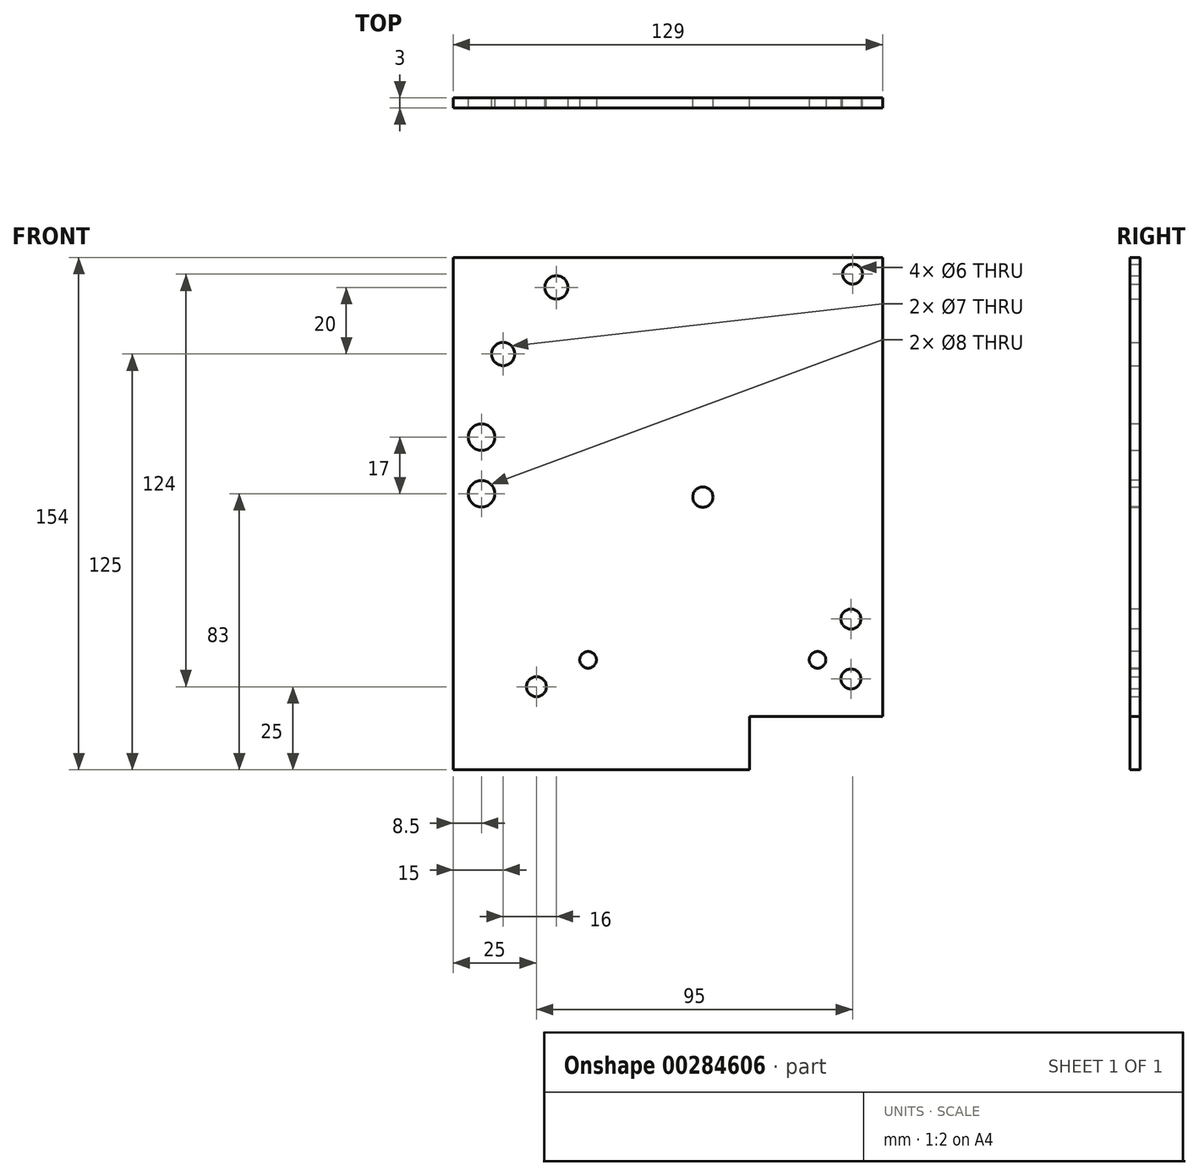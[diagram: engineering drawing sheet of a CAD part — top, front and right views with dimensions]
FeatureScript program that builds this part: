
annotation { "Feature Type Name" : "Feature", "Feature Type Description" : "" }
export const myFeature = defineFeature(function(context is Context, id is Id, definition is map)
    precondition{}
    {
        {
            var Q0;
            Q0=qCreatedBy(makeId("Front.planeOp"),FACE);
            var sketch = newSketch(context, id + "F0", { "sketchPlane" : qUnion([Q0])});
            skLineSegment(sketch, "E0", {"start": v(0, 0) * mm, "end": v(129, 0) * mm});
            skLineSegment(sketch, "E1", {"start": v(129, 0) * mm, "end": v(129, -138) * mm});
            skLineSegment(sketch, "E2", {"start": v(129, -138) * mm, "end": v(89, -138) * mm});
            skLineSegment(sketch, "E3", {"start": v(89, -138) * mm, "end": v(89, -154) * mm});
            skLineSegment(sketch, "E4", {"start": v(89, -154) * mm, "end": v(0, -154) * mm});
            skLineSegment(sketch, "E5", {"start": v(0, -154) * mm, "end": v(0, 0) * mm});
            skLineSegment(sketch, "E6", {"start": v(75, -154) * mm, "end": v(75, -127) * mm, "construction": true});
            skLineSegment(sketch, "E7", {"start": v(75, -127) * mm, "end": v(129, -127) * mm, "construction": true});
            skLineSegment(sketch, "E8", {"start": v(75, -127) * mm, "end": v(75, -72) * mm, "construction": true});
            skLineSegment(sketch, "E9", {"start": v(120, -138) * mm, "end": v(120, -99) * mm, "construction": true});
            skLineSegment(sketch, "E10", {"start": v(120, -99) * mm, "end": v(129, -99) * mm, "construction": true});
            skLineSegment(sketch, "E11", {"start": v(120, -99) * mm, "end": v(120, -5) * mm, "construction": true});
            skLineSegment(sketch, "E12", {"start": v(0, -9) * mm, "end": v(31, -9) * mm, "construction": true});
            skLineSegment(sketch, "E13", {"start": v(31, -9) * mm, "end": v(31, 0) * mm, "construction": true});
            skLineSegment(sketch, "E14", {"start": v(0, -29) * mm, "end": v(15, -29) * mm, "construction": true});
            skLineSegment(sketch, "E15", {"start": v(15, -29) * mm, "end": v(15, 0) * mm, "construction": true});
            skLineSegment(sketch, "E16", {"start": v(75, -129) * mm, "end": v(25, -129) * mm, "construction": true});
            skSolve(sketch);
        }
        {
            var Q0;
            Q0=makeQuery(id+"F0.imprint","IMPRINT",FACE,{"disambiguationData":[TD([[makeQuery(id+"F0.imprint","IMPRINT",EDGE,{"derivedFrom":sQuery(id+"F0.wireOp",EDGE,"E0")}),-1.0]])]});
            extrude(context, id + "F1", {"entities" : qUnion([Q0]), "depth" : 3 * mm});
        }
        {
            var Q0;
            Q0=sQuery(id+"F0.wireOp",VERTEX,"E14.end");
            var Q1;
            Q1=sQuery(id+"F0.wireOp",VERTEX,"E12.end");
            var Q2;
            Q2=makeQuery(id+"F1.opExtrude","SWEPT_BODY",BODY,{"disambiguationData":[OSD([sQuery(id+"F0.wireOp",EDGE,"E0"),sQuery(id+"F0.wireOp",EDGE,"E1"),sQuery(id+"F0.wireOp",EDGE,"E2"),sQuery(id+"F0.wireOp",EDGE,"E3"),sQuery(id+"F0.wireOp",EDGE,"E4"),sQuery(id+"F0.wireOp",EDGE,"E5")])]});
            hole(context, id + "F2", {"style" : HoleStyle.SIMPLE, "endStyle" : HoleEndStyle.THROUGH, "oppositeDirection" : true, "holeDiameter" : 7 * mm, "locations" : qUnion([Q0, Q1]), "scope" : qUnion([Q2]), "isTappedThrough" : true});
        }
        {
            var Q0;
            Q0=sQuery(id+"F0.wireOp",VERTEX,"E8.end");
            var Q1;
            Q1=makeQuery(id+"F1.opExtrude","SWEPT_BODY",BODY,{"disambiguationData":[OSD([sQuery(id+"F0.wireOp",EDGE,"E0"),sQuery(id+"F0.wireOp",EDGE,"E1"),sQuery(id+"F0.wireOp",EDGE,"E2"),sQuery(id+"F0.wireOp",EDGE,"E3"),sQuery(id+"F0.wireOp",EDGE,"E4"),sQuery(id+"F0.wireOp",EDGE,"E5")])]});
            hole(context, id + "F3", {"style" : HoleStyle.SIMPLE, "endStyle" : HoleEndStyle.THROUGH, "oppositeDirection" : true, "holeDiameter" : 6.1 * mm, "locations" : qUnion([Q0]), "scope" : qUnion([Q1]), "isTappedThrough" : true});
        }
        {
            var Q0;
            Q0=sQuery(id+"F0.wireOp",VERTEX,"E11.end");
            var Q1;
            Q1=sQuery(id+"F0.wireOp",VERTEX,"E16.end");
            var Q2;
            Q2=makeQuery(id+"F1.opExtrude","SWEPT_BODY",BODY,{"disambiguationData":[OSD([sQuery(id+"F0.wireOp",EDGE,"E0"),sQuery(id+"F0.wireOp",EDGE,"E1"),sQuery(id+"F0.wireOp",EDGE,"E2"),sQuery(id+"F0.wireOp",EDGE,"E3"),sQuery(id+"F0.wireOp",EDGE,"E4"),sQuery(id+"F0.wireOp",EDGE,"E5")])]});
            hole(context, id + "F4", {"style" : HoleStyle.SIMPLE, "endStyle" : HoleEndStyle.THROUGH, "oppositeDirection" : true, "holeDiameter" : 6 * mm, "locations" : qUnion([Q0, Q1]), "scope" : qUnion([Q2]), "isTappedThrough" : true});
        }
        {
            var Q0;
            Q0=makeQuery(id+"F1.opExtrude","CAP_FACE",FACE,{"disambiguationData":[OSD([sQuery(id+"F0.wireOp",EDGE,"E0"),sQuery(id+"F0.wireOp",EDGE,"E1"),sQuery(id+"F0.wireOp",EDGE,"E2"),sQuery(id+"F0.wireOp",EDGE,"E3"),sQuery(id+"F0.wireOp",EDGE,"E4"),sQuery(id+"F0.wireOp",EDGE,"E5")])],"isStart":false});
            var sketch = newSketch(context, id + "F5", { "sketchPlane" : qUnion([Q0])});
            skLineSegment(sketch, "E17", {"start": v(75, -127) * mm, "end": v(109.47, -120.92) * mm, "construction": true});
            skLineSegment(sketch, "E18", {"start": v(75, -127) * mm, "end": v(77, -127) * mm, "construction": true});
            skLineSegment(sketch, "E19", {"start": v(75, -127) * mm, "end": v(40.53, -120.92) * mm, "construction": true});
            skLineSegment(sketch, "E20", {"start": v(8.5, -154) * mm, "end": v(8.5, -54) * mm, "construction": true});
            skLineSegment(sketch, "E21", {"start": v(8.5, -54) * mm, "end": v(0, -54) * mm, "construction": true});
            skPoint(sketch, "E22", {"position": v(8.5, -71) * mm});
            skLineSegment(sketch, "E23", {"start": v(119.5, -138) * mm, "end": v(119.5, -108.67) * mm, "construction": true});
            skLineSegment(sketch, "E24", {"start": v(119.5, -108.67) * mm, "end": v(129, -108.67) * mm, "construction": true});
            skPoint(sketch, "E25", {"position": v(119.5, -126.67) * mm});
            skSolve(sketch);
        }
        {
            var Q0;
            Q0=sQuery(id+"F5.wireOp",VERTEX,"E19.end");
            var Q1;
            Q1=sQuery(id+"F5.wireOp",VERTEX,"E17.end");
            var Q2;
            Q2=makeQuery(id+"F1.opExtrude","SWEPT_BODY",BODY,{"disambiguationData":[OSD([sQuery(id+"F0.wireOp",EDGE,"E0"),sQuery(id+"F0.wireOp",EDGE,"E1"),sQuery(id+"F0.wireOp",EDGE,"E2"),sQuery(id+"F0.wireOp",EDGE,"E3"),sQuery(id+"F0.wireOp",EDGE,"E4"),sQuery(id+"F0.wireOp",EDGE,"E5")])]});
            hole(context, id + "F6", {"style" : HoleStyle.SIMPLE, "endStyle" : HoleEndStyle.THROUGH, "holeDiameter" : 5 * mm, "locations" : qUnion([Q0, Q1]), "scope" : qUnion([Q2]), "isTappedThrough" : true});
        }
        {
            var Q0;
            Q0=sQuery(id+"F5.wireOp",VERTEX,"E22");
            var Q1;
            Q1=sQuery(id+"F5.wireOp",VERTEX,"E21.start");
            var Q2;
            Q2=makeQuery(id+"F1.opExtrude","SWEPT_BODY",BODY,{"disambiguationData":[OSD([sQuery(id+"F0.wireOp",EDGE,"E0"),sQuery(id+"F0.wireOp",EDGE,"E1"),sQuery(id+"F0.wireOp",EDGE,"E2"),sQuery(id+"F0.wireOp",EDGE,"E3"),sQuery(id+"F0.wireOp",EDGE,"E4"),sQuery(id+"F0.wireOp",EDGE,"E5")])]});
            hole(context, id + "F7", {"style" : HoleStyle.SIMPLE, "endStyle" : HoleEndStyle.THROUGH, "holeDiameter" : 8 * mm, "locations" : qUnion([Q0, Q1]), "scope" : qUnion([Q2]), "isTappedThrough" : true});
        }
        {
            var Q0;
            Q0=sQuery(id+"F5.wireOp",VERTEX,"E24.start");
            var Q1;
            Q1=sQuery(id+"F5.wireOp",VERTEX,"E25");
            var Q2;
            Q2=makeQuery(id+"F1.opExtrude","SWEPT_BODY",BODY,{"disambiguationData":[OSD([sQuery(id+"F0.wireOp",EDGE,"E0"),sQuery(id+"F0.wireOp",EDGE,"E1"),sQuery(id+"F0.wireOp",EDGE,"E2"),sQuery(id+"F0.wireOp",EDGE,"E3"),sQuery(id+"F0.wireOp",EDGE,"E4"),sQuery(id+"F0.wireOp",EDGE,"E5")])]});
            hole(context, id + "F8", {"style" : HoleStyle.SIMPLE, "endStyle" : HoleEndStyle.THROUGH, "holeDiameter" : 6 * mm, "locations" : qUnion([Q0, Q1]), "scope" : qUnion([Q2]), "isTappedThrough" : true});
        }
    });
